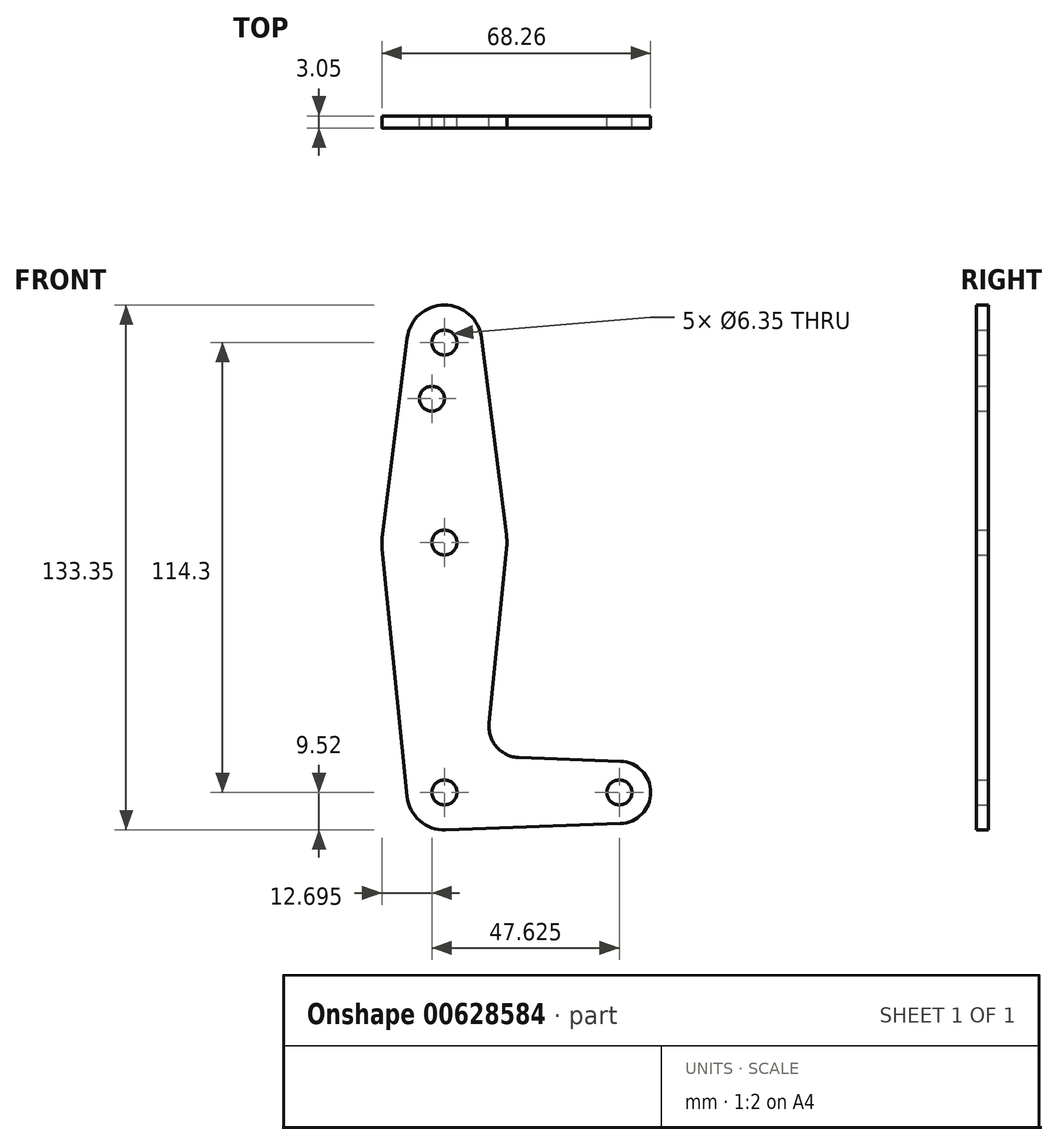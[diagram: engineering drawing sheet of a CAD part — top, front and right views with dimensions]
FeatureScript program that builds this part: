
annotation { "Feature Type Name" : "Feature", "Feature Type Description" : "" }
export const myFeature = defineFeature(function(context is Context, id is Id, definition is map)
    precondition{}
    {
        {
            var Q0;
            Q0=qCreatedBy(makeId("Front.planeOp"),FACE);
            var sketch = newSketch(context, id + "F0", { "sketchPlane" : qUnion([Q0])});
            skLineSegment(sketch, "E0", {"start": v(0, 0) * mm, "end": v(0, 114.3) * mm, "construction": true});
            skLineSegment(sketch, "E1", {"start": v(0, 0) * mm, "end": v(44.45, 0) * mm, "construction": true});
            skCircle(sketch, "E2", {"center": v(0, 114.3) * mm, "radius": 9.53 * mm});
            skCircle(sketch, "E3", {"center": v(0, 63.5) * mm, "radius": 15.88 * mm});
            skCircle(sketch, "E4", {"center": v(0, 0) * mm, "radius": 9.53 * mm});
            skCircle(sketch, "E5", {"center": v(44.45, 0) * mm, "radius": 7.94 * mm});
            skLineSegment(sketch, "E6", {"start": v(-15.8, 61.91) * mm, "end": v(-9.48, -0.95) * mm});
            skLineSegment(sketch, "E7", {"start": v(15.8, 61.91) * mm, "end": v(11.34, 17.6) * mm});
            skLineSegment(sketch, "E8", {"start": v(-9.45, 115.5) * mm, "end": v(-15.75, 65.48) * mm});
            skLineSegment(sketch, "E9", {"start": v(9.45, 115.5) * mm, "end": v(15.75, 65.48) * mm});
            skLineSegment(sketch, "E10", {"start": v(44.73, 7.93) * mm, "end": v(18.97, 8.85) * mm});
            skLineSegment(sketch, "E11", {"start": v(44.73, -7.93) * mm, "end": v(0.34, -9.52) * mm});
            skCircle(sketch, "E12", {"center": v(0, 114.3) * mm, "radius": 3.18 * mm});
            skCircle(sketch, "E13", {"center": v(-3.18, 100.03) * mm, "radius": 3.18 * mm});
            skCircle(sketch, "E14", {"center": v(0, 63.5) * mm, "radius": 3.18 * mm});
            skCircle(sketch, "E15", {"center": v(0, 0) * mm, "radius": 3.18 * mm});
            skCircle(sketch, "E16", {"center": v(44.45, 0) * mm, "radius": 3.18 * mm});
            skArc(sketch, "E17.filletArc", {"start": v(11.34, 17.6) * mm, "mid": v(13.26, 11.57) * mm, "end": v(18.97, 8.85) * mm});
            skSolve(sketch);
        }
        {
            var Q0;
            Q0=makeQuery(id+"F0.imprint","IMPRINT",FACE,{"disambiguationData":[TD([[makeQuery(id+"F0.imprint","IMPRINT",EDGE,{"derivedFrom":sQuery(id+"F0.wireOp",EDGE,"E12")}),-1.0]])]});
            var Q1;
            {var subQ1=sQuery(id+"F0.wireOp",EDGE,"E8");Q1=makeQuery(id+"F0.imprint","IMPRINT",FACE,{"disambiguationData":[TD([[makeQuery(id+"F0.imprint","IMPRINT",EDGE,{"derivedFrom":subQ1}),1.0]])]});}
            var Q2;
            Q2=makeQuery(id+"F0.imprint","IMPRINT",FACE,{"disambiguationData":[TD([[makeQuery(id+"F0.imprint","IMPRINT",EDGE,{"derivedFrom":sQuery(id+"F0.wireOp",EDGE,"E14")}),-1.0]])]});
            var Q3;
            {var subQ0=sQuery(id+"F0.wireOp",EDGE,"E6");Q3=makeQuery(id+"F0.imprint","IMPRINT",FACE,{"disambiguationData":[TD([[makeQuery(id+"F0.imprint","IMPRINT",EDGE,{"derivedFrom":subQ0}),1.0]])]});}
            var Q4;
            Q4=makeQuery(id+"F0.imprint","IMPRINT",FACE,{"disambiguationData":[TD([[makeQuery(id+"F0.imprint","IMPRINT",EDGE,{"derivedFrom":sQuery(id+"F0.wireOp",EDGE,"E15")}),-1.0]])]});
            var Q5;
            Q5=makeQuery(id+"F0.imprint","IMPRINT",FACE,{"disambiguationData":[TD([[makeQuery(id+"F0.imprint","IMPRINT",EDGE,{"derivedFrom":sQuery(id+"F0.wireOp",EDGE,"E16")}),-1.0]])]});
            extrude(context, id + "F1", {"entities" : qUnion([Q0, Q1, Q2, Q3, Q4, Q5]), "depth" : 3.05 * mm, "offsetDistance" : 25.4 * mm});
        }
    });
